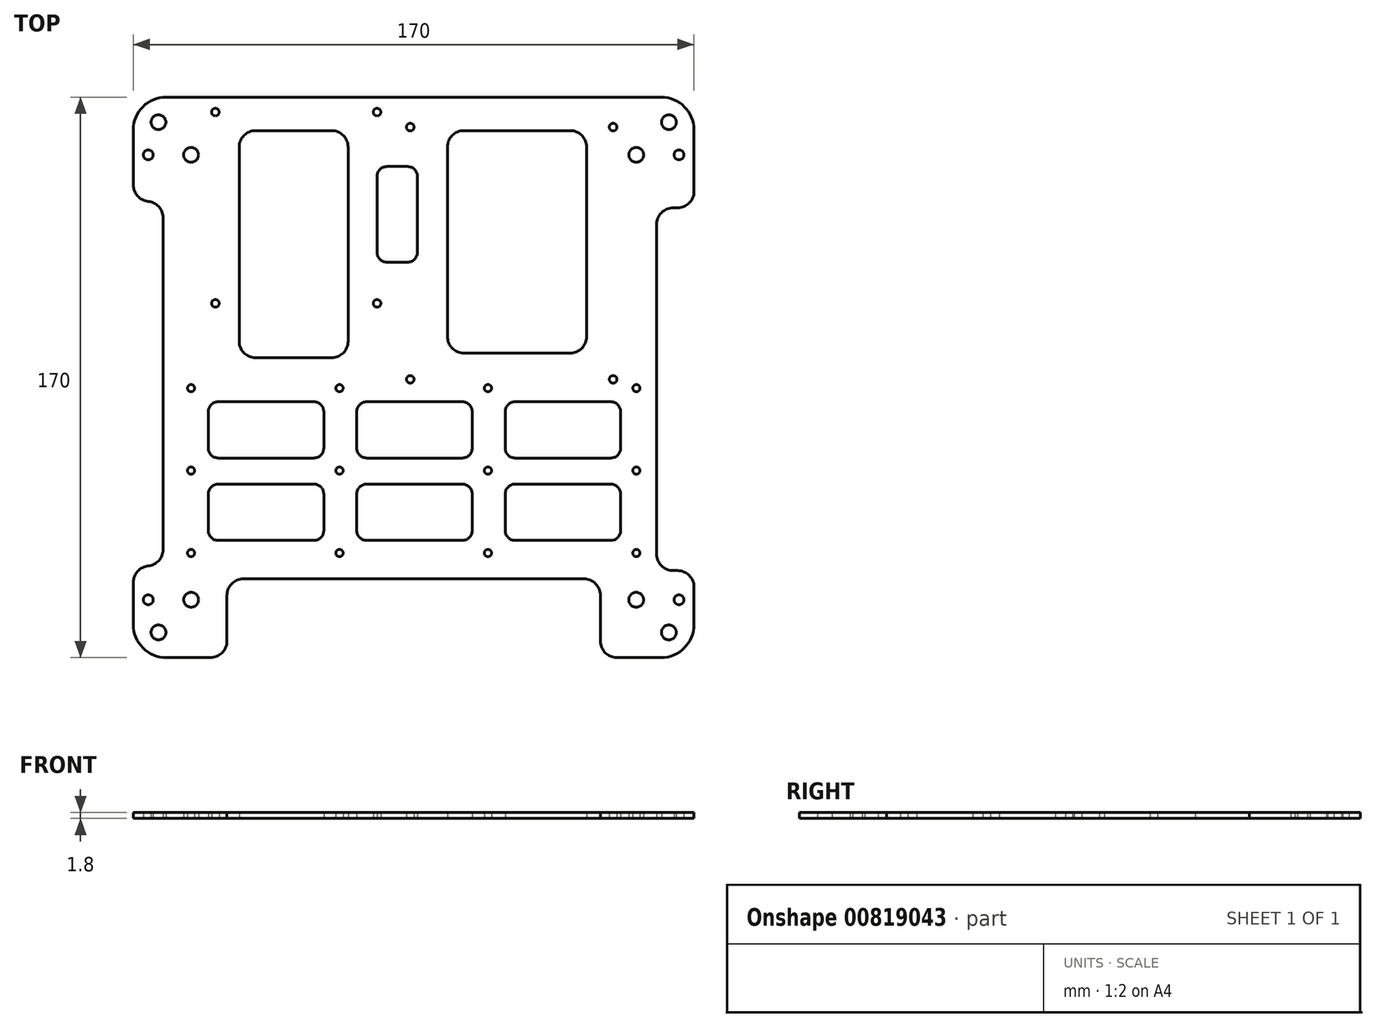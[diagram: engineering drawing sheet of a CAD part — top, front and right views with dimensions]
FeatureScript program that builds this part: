
annotation { "Feature Type Name" : "Feature", "Feature Type Description" : "" }
export const myFeature = defineFeature(function(context is Context, id is Id, definition is map)
    precondition{}
    {
        {
            var Q0;
            Q0=qCreatedBy(makeId("Top.planeOp"),FACE);
            var sketch = newSketch(context, id + "F0", { "sketchPlane" : qUnion([Q0])});
            skLineSegment(sketch, "E0.bottom", {"start": v(-100, -100) * mm, "end": v(100, -100) * mm, "construction": true});
            skLineSegment(sketch, "E0.top", {"start": v(-100, 100) * mm, "end": v(100, 100) * mm, "construction": true});
            skLineSegment(sketch, "E0.left", {"start": v(-100, -100) * mm, "end": v(-100, 100) * mm, "construction": true});
            skLineSegment(sketch, "E0.right", {"start": v(100, -100) * mm, "end": v(100, 100) * mm, "construction": true});
            skPoint(sketch, "E0.middle", {"position": v(0, 0) * mm});
            skCircle(sketch, "E1", {"center": v(-100, 100) * mm, "radius": 2.5 * mm, "construction": true});
            skCircle(sketch, "E2", {"center": v(100, 100) * mm, "radius": 2.5 * mm, "construction": true});
            skCircle(sketch, "E3", {"center": v(100, -100) * mm, "radius": 2.5 * mm, "construction": true});
            skCircle(sketch, "E4", {"center": v(-100, -100) * mm, "radius": 2.5 * mm, "construction": true});
            skLineSegment(sketch, "E5", {"start": v(-100, 100) * mm, "end": v(-77.37, 77.37) * mm, "construction": true});
            skLineSegment(sketch, "E6", {"start": v(-77.37, 77.37) * mm, "end": v(-67.47, 67.47) * mm, "construction": true});
            skCircle(sketch, "E7", {"center": v(-77.37, 77.37) * mm, "radius": 2.25 * mm});
            skCircle(sketch, "E8", {"center": v(-67.47, 67.47) * mm, "radius": 2.25 * mm});
            skLineSegment(sketch, "E9.bottom", {"start": v(-85, 85) * mm, "end": v(85, 85) * mm});
            skLineSegment(sketch, "E9.top", {"start": v(-85, -85) * mm, "end": v(85, -85) * mm});
            skLineSegment(sketch, "E9.left", {"start": v(-85, 85) * mm, "end": v(-85, -85) * mm});
            skLineSegment(sketch, "E9.right", {"start": v(85, 85) * mm, "end": v(85, -85) * mm});
            skLineSegment(sketch, "E10.bottom", {"start": v(-1.03, -0.6) * mm, "end": v(60.47, -0.6) * mm, "construction": true});
            skLineSegment(sketch, "E10.top", {"start": v(-1.03, 75.9) * mm, "end": v(60.47, 75.9) * mm, "construction": true});
            skLineSegment(sketch, "E10.left", {"start": v(-1.03, -0.6) * mm, "end": v(-1.03, 75.9) * mm, "construction": true});
            skLineSegment(sketch, "E10.right", {"start": v(60.47, -0.6) * mm, "end": v(60.47, 75.9) * mm, "construction": true});
            skPoint(sketch, "E10.middle", {"position": v(29.72, 37.64) * mm});
            skLineSegment(sketch, "E11.bottom", {"start": v(-5.28, -12.36) * mm, "end": v(64.72, -12.36) * mm, "construction": true});
            skLineSegment(sketch, "E11.top", {"start": v(-5.28, 87.64) * mm, "end": v(64.72, 87.64) * mm, "construction": true});
            skLineSegment(sketch, "E11.left", {"start": v(-5.28, -12.36) * mm, "end": v(-5.28, 87.64) * mm, "construction": true});
            skLineSegment(sketch, "E11.right", {"start": v(64.72, -12.36) * mm, "end": v(64.72, 87.64) * mm, "construction": true});
            skLineSegment(sketch, "E12.bottom", {"start": v(-11.1, 22.43) * mm, "end": v(-60.1, 22.43) * mm, "construction": true});
            skLineSegment(sketch, "E12.top", {"start": v(-11.1, 80.43) * mm, "end": v(-60.1, 80.43) * mm, "construction": true});
            skLineSegment(sketch, "E12.left", {"start": v(-11.1, 22.43) * mm, "end": v(-11.1, 80.43) * mm, "construction": true});
            skLineSegment(sketch, "E12.right", {"start": v(-60.1, 22.43) * mm, "end": v(-60.1, 80.43) * mm, "construction": true});
            skPoint(sketch, "E12.middle", {"position": v(-35.6, 51.43) * mm});
            skLineSegment(sketch, "E13.bottom", {"start": v(-7.6, 96.43) * mm, "end": v(-63.6, 96.43) * mm, "construction": true});
            skLineSegment(sketch, "E13.top", {"start": v(-7.6, 6.43) * mm, "end": v(-63.6, 6.43) * mm, "construction": true});
            skLineSegment(sketch, "E13.left", {"start": v(-7.6, 96.43) * mm, "end": v(-7.6, 6.43) * mm, "construction": true});
            skLineSegment(sketch, "E13.right", {"start": v(-63.6, 96.43) * mm, "end": v(-63.6, 6.43) * mm, "construction": true});
            skLineSegment(sketch, "E14", {"start": v(0, 0) * mm, "end": v(0, 19) * mm, "construction": true});
            skLineSegment(sketch, "E15", {"start": v(0, 0) * mm, "end": v(16.24, 0) * mm, "construction": true});
            skCircle(sketch, "E16.MirrorC", {"center": v(77.37, 77.37) * mm, "radius": 2.25 * mm});
            skCircle(sketch, "E17.MirrorC", {"center": v(67.47, 67.47) * mm, "radius": 2.25 * mm});
            skCircle(sketch, "E18.MirrorC", {"center": v(-67.47, -67.47) * mm, "radius": 2.25 * mm});
            skCircle(sketch, "E19.MirrorC", {"center": v(-77.37, -77.37) * mm, "radius": 2.25 * mm});
            skCircle(sketch, "E20.MirrorC", {"center": v(77.37, -77.37) * mm, "radius": 2.25 * mm});
            skCircle(sketch, "E21.MirrorC", {"center": v(67.47, -67.47) * mm, "radius": 2.25 * mm});
            skCircle(sketch, "E22", {"center": v(-60.1, 80.43) * mm, "radius": 1.15 * mm});
            skCircle(sketch, "E23", {"center": v(-11.1, 80.43) * mm, "radius": 1.15 * mm});
            skCircle(sketch, "E24", {"center": v(-11.1, 22.43) * mm, "radius": 1.15 * mm});
            skCircle(sketch, "E25", {"center": v(-60.1, 22.43) * mm, "radius": 1.15 * mm});
            skCircle(sketch, "E26", {"center": v(-1.03, 75.9) * mm, "radius": 1.15 * mm});
            skCircle(sketch, "E27", {"center": v(60.47, 75.9) * mm, "radius": 1.15 * mm});
            skCircle(sketch, "E28", {"center": v(60.47, -0.6) * mm, "radius": 1.15 * mm});
            skCircle(sketch, "E29", {"center": v(-1.03, -0.6) * mm, "radius": 1.15 * mm});
            skCircle(sketch, "E30", {"center": v(-80.45, 67.47) * mm, "radius": 1.5 * mm});
            skCircle(sketch, "E31.MirrorC", {"center": v(80.45, 67.47) * mm, "radius": 1.5 * mm});
            skCircle(sketch, "E32.MirrorC", {"center": v(-80.45, -67.47) * mm, "radius": 1.5 * mm});
            skCircle(sketch, "E33.MirrorC", {"center": v(80.45, -67.47) * mm, "radius": 1.5 * mm});
            skSolve(sketch);
        }
        {
            var Q0;
            Q0 = qSketchRegion(id + "F0", true);
            extrude(context, id + "F1", {"entities" : qUnion([Q0]), "depth" : 1.8 * mm, "offsetDistance" : 25 * mm});
        }
        {
            var Q0;
            Q0=makeQuery(id+"F1.opExtrude","SWEPT_EDGE",EDGE,{"disambiguationData":[OSD([sQuery(id+"F0.wireOp",EDGE,"E9.bottom"),sQuery(id+"F0.wireOp",EDGE,"E9.left")])]});
            var Q1;
            Q1=makeQuery(id+"F1.opExtrude","SWEPT_EDGE",EDGE,{"disambiguationData":[OSD([sQuery(id+"F0.wireOp",EDGE,"E9.bottom"),sQuery(id+"F0.wireOp",EDGE,"E9.right")])]});
            var Q2;
            Q2=makeQuery(id+"F1.opExtrude","SWEPT_EDGE",EDGE,{"disambiguationData":[OSD([sQuery(id+"F0.wireOp",EDGE,"E9.top"),sQuery(id+"F0.wireOp",EDGE,"E9.right")])]});
            var Q3;
            Q3=makeQuery(id+"F1.opExtrude","SWEPT_EDGE",EDGE,{"disambiguationData":[OSD([sQuery(id+"F0.wireOp",EDGE,"E9.top"),sQuery(id+"F0.wireOp",EDGE,"E9.left")])]});
            fillet(context, id + "F2", {"entities" : qUnion([Q0, Q1, Q2, Q3]), "radius" : 10 * mm, "tangentPropagation" : true, "allowEdgeOverflow" : false});
        }
        {
            var Q0;
            Q0=qCreatedBy(makeId("Top.planeOp"),FACE);
            var sketch = newSketch(context, id + "F3", { "sketchPlane" : qUnion([Q0])});
            skLineSegment(sketch, "E34", {"start": v(15.24, 7.36) * mm, "end": v(28.1, 7.36) * mm});
            skCircle(sketch, "E35", {"center": v(-67.48, -53.3) * mm, "radius": 1.1 * mm});
            skLineSegment(sketch, "E36", {"start": v(-67.48, -53.3) * mm, "end": v(-67.48, -28.3) * mm, "construction": true});
            skCircle(sketch, "E37", {"center": v(-67.48, -28.3) * mm, "radius": 1.1 * mm});
            skLineSegment(sketch, "E38.bottom", {"start": v(-59.25, -32.4) * mm, "end": v(-30.25, -32.4) * mm});
            skLineSegment(sketch, "E38.top", {"start": v(-59.25, -49.48) * mm, "end": v(-30.25, -49.48) * mm});
            skLineSegment(sketch, "E38.left", {"start": v(-62.25, -35.4) * mm, "end": v(-62.25, -46.48) * mm});
            skLineSegment(sketch, "E38.right", {"start": v(-27.25, -35.4) * mm, "end": v(-27.25, -46.48) * mm});
            skPoint(sketch, "E39.visualSharp", {"position": v(-62.25, -32.4) * mm});
            skArc(sketch, "E39.filletArc", {"start": v(-59.25, -32.4) * mm, "mid": v(-61.37, -33.29) * mm, "end": v(-62.25, -35.4) * mm});
            skPoint(sketch, "E40.visualSharp", {"position": v(-27.25, -32.4) * mm});
            skArc(sketch, "E40.filletArc", {"start": v(-27.25, -35.4) * mm, "mid": v(-28.13, -33.29) * mm, "end": v(-30.25, -32.4) * mm});
            skPoint(sketch, "E41.visualSharp", {"position": v(-27.25, -49.48) * mm});
            skArc(sketch, "E41.filletArc", {"start": v(-30.25, -49.48) * mm, "mid": v(-28.13, -48.6) * mm, "end": v(-27.25, -46.48) * mm});
            skPoint(sketch, "E42.visualSharp", {"position": v(-62.25, -49.48) * mm});
            skArc(sketch, "E42.filletArc", {"start": v(-62.25, -46.48) * mm, "mid": v(-61.37, -48.6) * mm, "end": v(-59.25, -49.48) * mm});
            skLineSegment(sketch, "E43.0.1.0", {"start": v(-27.25, -10.4) * mm, "end": v(-27.25, -21.48) * mm});
            skLineSegment(sketch, "E43.0.1.1", {"start": v(-59.25, -7.4) * mm, "end": v(-30.25, -7.4) * mm});
            skLineSegment(sketch, "E43.0.1.2", {"start": v(-67.48, -28.3) * mm, "end": v(-67.48, -3.3) * mm, "construction": true});
            skLineSegment(sketch, "E43.0.1.3", {"start": v(-62.25, -10.4) * mm, "end": v(-62.25, -21.48) * mm});
            skLineSegment(sketch, "E43.0.1.4", {"start": v(-59.25, -24.48) * mm, "end": v(-30.25, -24.48) * mm});
            skPoint(sketch, "E43.0.1.5", {"position": v(-62.25, -24.48) * mm});
            skPoint(sketch, "E43.0.1.6", {"position": v(-27.25, -24.48) * mm});
            skPoint(sketch, "E43.0.1.7", {"position": v(-27.25, -7.4) * mm});
            skPoint(sketch, "E43.0.1.8", {"position": v(-62.25, -7.4) * mm});
            skArc(sketch, "E43.0.1.9", {"start": v(-59.25, -7.4) * mm, "mid": v(-61.37, -8.29) * mm, "end": v(-62.25, -10.4) * mm});
            skArc(sketch, "E43.0.1.10", {"start": v(-30.25, -24.48) * mm, "mid": v(-28.13, -23.6) * mm, "end": v(-27.25, -21.48) * mm});
            skArc(sketch, "E43.0.1.11", {"start": v(-62.25, -21.48) * mm, "mid": v(-61.37, -23.6) * mm, "end": v(-59.25, -24.48) * mm});
            skCircle(sketch, "E43.0.1.12", {"center": v(-67.48, -3.3) * mm, "radius": 1.1 * mm});
            skArc(sketch, "E43.0.1.14", {"start": v(-27.25, -10.4) * mm, "mid": v(-28.13, -8.29) * mm, "end": v(-30.25, -7.4) * mm});
            skLineSegment(sketch, "E43.1.0.0", {"start": v(17.75, -35.4) * mm, "end": v(17.75, -46.48) * mm});
            skLineSegment(sketch, "E43.1.0.1", {"start": v(-14.25, -32.4) * mm, "end": v(14.75, -32.4) * mm});
            skLineSegment(sketch, "E43.1.0.2", {"start": v(-22.48, -53.3) * mm, "end": v(-22.48, -28.3) * mm, "construction": true});
            skLineSegment(sketch, "E43.1.0.3", {"start": v(-17.25, -35.4) * mm, "end": v(-17.25, -46.48) * mm});
            skLineSegment(sketch, "E43.1.0.4", {"start": v(-14.25, -49.48) * mm, "end": v(14.75, -49.48) * mm});
            skPoint(sketch, "E43.1.0.5", {"position": v(-17.25, -49.48) * mm});
            skPoint(sketch, "E43.1.0.6", {"position": v(17.75, -49.48) * mm});
            skPoint(sketch, "E43.1.0.7", {"position": v(17.75, -32.4) * mm});
            skPoint(sketch, "E43.1.0.8", {"position": v(-17.25, -32.4) * mm});
            skArc(sketch, "E43.1.0.9", {"start": v(-14.25, -32.4) * mm, "mid": v(-16.37, -33.29) * mm, "end": v(-17.25, -35.4) * mm});
            skArc(sketch, "E43.1.0.10", {"start": v(14.75, -49.48) * mm, "mid": v(16.87, -48.6) * mm, "end": v(17.75, -46.48) * mm});
            skArc(sketch, "E43.1.0.11", {"start": v(-17.25, -46.48) * mm, "mid": v(-16.37, -48.6) * mm, "end": v(-14.25, -49.48) * mm});
            skCircle(sketch, "E43.1.0.12", {"center": v(-22.48, -28.3) * mm, "radius": 1.1 * mm});
            skCircle(sketch, "E43.1.0.13", {"center": v(-22.48, -53.3) * mm, "radius": 1.1 * mm});
            skArc(sketch, "E43.1.0.14", {"start": v(17.75, -35.4) * mm, "mid": v(16.87, -33.29) * mm, "end": v(14.75, -32.4) * mm});
            skLineSegment(sketch, "E43.1.1.0", {"start": v(17.75, -10.4) * mm, "end": v(17.75, -21.48) * mm});
            skLineSegment(sketch, "E43.1.1.1", {"start": v(-14.25, -7.4) * mm, "end": v(14.75, -7.4) * mm});
            skLineSegment(sketch, "E43.1.1.2", {"start": v(-22.48, -28.3) * mm, "end": v(-22.48, -3.3) * mm, "construction": true});
            skLineSegment(sketch, "E43.1.1.3", {"start": v(-17.25, -10.4) * mm, "end": v(-17.25, -21.48) * mm});
            skLineSegment(sketch, "E43.1.1.4", {"start": v(-14.25, -24.48) * mm, "end": v(14.75, -24.48) * mm});
            skPoint(sketch, "E43.1.1.5", {"position": v(-17.25, -24.48) * mm});
            skPoint(sketch, "E43.1.1.6", {"position": v(17.75, -24.48) * mm});
            skPoint(sketch, "E43.1.1.7", {"position": v(17.75, -7.4) * mm});
            skPoint(sketch, "E43.1.1.8", {"position": v(-17.25, -7.4) * mm});
            skArc(sketch, "E43.1.1.9", {"start": v(-14.25, -7.4) * mm, "mid": v(-16.37, -8.29) * mm, "end": v(-17.25, -10.4) * mm});
            skArc(sketch, "E43.1.1.10", {"start": v(14.75, -24.48) * mm, "mid": v(16.87, -23.6) * mm, "end": v(17.75, -21.48) * mm});
            skArc(sketch, "E43.1.1.11", {"start": v(-17.25, -21.48) * mm, "mid": v(-16.37, -23.6) * mm, "end": v(-14.25, -24.48) * mm});
            skCircle(sketch, "E43.1.1.12", {"center": v(-22.48, -3.3) * mm, "radius": 1.1 * mm});
            skCircle(sketch, "E43.1.1.13", {"center": v(-22.48, -28.3) * mm, "radius": 1.1 * mm});
            skArc(sketch, "E43.1.1.14", {"start": v(17.75, -10.4) * mm, "mid": v(16.87, -8.29) * mm, "end": v(14.75, -7.4) * mm});
            skLineSegment(sketch, "E43.2.0.0", {"start": v(62.75, -35.4) * mm, "end": v(62.75, -46.48) * mm});
            skLineSegment(sketch, "E43.2.0.1", {"start": v(30.75, -32.4) * mm, "end": v(59.75, -32.4) * mm});
            skLineSegment(sketch, "E43.2.0.2", {"start": v(22.52, -53.3) * mm, "end": v(22.52, -28.3) * mm, "construction": true});
            skLineSegment(sketch, "E43.2.0.3", {"start": v(27.75, -35.4) * mm, "end": v(27.75, -46.48) * mm});
            skLineSegment(sketch, "E43.2.0.4", {"start": v(30.75, -49.48) * mm, "end": v(59.75, -49.48) * mm});
            skPoint(sketch, "E43.2.0.5", {"position": v(27.75, -49.48) * mm});
            skPoint(sketch, "E43.2.0.6", {"position": v(62.75, -49.48) * mm});
            skPoint(sketch, "E43.2.0.7", {"position": v(62.75, -32.4) * mm});
            skPoint(sketch, "E43.2.0.8", {"position": v(27.75, -32.4) * mm});
            skArc(sketch, "E43.2.0.9", {"start": v(30.75, -32.4) * mm, "mid": v(28.63, -33.29) * mm, "end": v(27.75, -35.4) * mm});
            skArc(sketch, "E43.2.0.10", {"start": v(59.75, -49.48) * mm, "mid": v(61.87, -48.6) * mm, "end": v(62.75, -46.48) * mm});
            skArc(sketch, "E43.2.0.11", {"start": v(27.75, -46.48) * mm, "mid": v(28.63, -48.6) * mm, "end": v(30.75, -49.48) * mm});
            skCircle(sketch, "E43.2.0.12", {"center": v(22.52, -28.3) * mm, "radius": 1.1 * mm});
            skCircle(sketch, "E43.2.0.13", {"center": v(22.52, -53.3) * mm, "radius": 1.1 * mm});
            skArc(sketch, "E43.2.0.14", {"start": v(62.75, -35.4) * mm, "mid": v(61.87, -33.29) * mm, "end": v(59.75, -32.4) * mm});
            skLineSegment(sketch, "E43.2.1.0", {"start": v(62.75, -10.4) * mm, "end": v(62.75, -21.48) * mm});
            skLineSegment(sketch, "E43.2.1.1", {"start": v(30.75, -7.4) * mm, "end": v(59.75, -7.4) * mm});
            skLineSegment(sketch, "E43.2.1.2", {"start": v(22.52, -28.3) * mm, "end": v(22.52, -3.3) * mm, "construction": true});
            skLineSegment(sketch, "E43.2.1.3", {"start": v(27.75, -10.4) * mm, "end": v(27.75, -21.48) * mm});
            skLineSegment(sketch, "E43.2.1.4", {"start": v(30.75, -24.48) * mm, "end": v(59.75, -24.48) * mm});
            skPoint(sketch, "E43.2.1.5", {"position": v(27.75, -24.48) * mm});
            skPoint(sketch, "E43.2.1.6", {"position": v(62.75, -24.48) * mm});
            skPoint(sketch, "E43.2.1.7", {"position": v(62.75, -7.4) * mm});
            skPoint(sketch, "E43.2.1.8", {"position": v(27.75, -7.4) * mm});
            skArc(sketch, "E43.2.1.9", {"start": v(30.75, -7.4) * mm, "mid": v(28.63, -8.29) * mm, "end": v(27.75, -10.4) * mm});
            skArc(sketch, "E43.2.1.10", {"start": v(59.75, -24.48) * mm, "mid": v(61.87, -23.6) * mm, "end": v(62.75, -21.48) * mm});
            skArc(sketch, "E43.2.1.11", {"start": v(27.75, -21.48) * mm, "mid": v(28.63, -23.6) * mm, "end": v(30.75, -24.48) * mm});
            skCircle(sketch, "E43.2.1.12", {"center": v(22.52, -3.3) * mm, "radius": 1.1 * mm});
            skCircle(sketch, "E43.2.1.13", {"center": v(22.52, -28.3) * mm, "radius": 1.1 * mm});
            skArc(sketch, "E43.2.1.14", {"start": v(62.75, -10.4) * mm, "mid": v(61.87, -8.29) * mm, "end": v(59.75, -7.4) * mm});
            skLineSegment(sketch, "E43.3.0.0", {"start": v(107.75, -35.4) * mm, "end": v(107.75, -46.48) * mm, "construction": true});
            skLineSegment(sketch, "E43.3.0.1", {"start": v(75.75, -32.4) * mm, "end": v(104.75, -32.4) * mm, "construction": true});
            skLineSegment(sketch, "E43.3.0.2", {"start": v(67.52, -53.3) * mm, "end": v(67.52, -28.3) * mm, "construction": true});
            skLineSegment(sketch, "E43.3.0.3", {"start": v(72.75, -35.4) * mm, "end": v(72.75, -46.48) * mm, "construction": true});
            skLineSegment(sketch, "E43.3.0.4", {"start": v(75.75, -49.48) * mm, "end": v(104.75, -49.48) * mm, "construction": true});
            skPoint(sketch, "E43.3.0.5", {"position": v(72.75, -49.48) * mm});
            skPoint(sketch, "E43.3.0.6", {"position": v(107.75, -49.48) * mm});
            skPoint(sketch, "E43.3.0.7", {"position": v(107.75, -32.4) * mm});
            skPoint(sketch, "E43.3.0.8", {"position": v(72.75, -32.4) * mm});
            skArc(sketch, "E43.3.0.9", {"start": v(75.75, -32.4) * mm, "mid": v(73.63, -33.29) * mm, "end": v(72.75, -35.4) * mm, "construction": true});
            skArc(sketch, "E43.3.0.10", {"start": v(104.75, -49.48) * mm, "mid": v(106.87, -48.6) * mm, "end": v(107.75, -46.48) * mm, "construction": true});
            skArc(sketch, "E43.3.0.11", {"start": v(72.75, -46.48) * mm, "mid": v(73.63, -48.6) * mm, "end": v(75.75, -49.48) * mm, "construction": true});
            skCircle(sketch, "E43.3.0.12", {"center": v(67.52, -28.3) * mm, "radius": 1.1 * mm});
            skCircle(sketch, "E43.3.0.13", {"center": v(67.52, -53.3) * mm, "radius": 1.1 * mm});
            skArc(sketch, "E43.3.0.14", {"start": v(107.75, -35.4) * mm, "mid": v(106.87, -33.29) * mm, "end": v(104.75, -32.4) * mm, "construction": true});
            skLineSegment(sketch, "E43.3.1.0", {"start": v(107.75, -10.4) * mm, "end": v(107.75, -21.48) * mm, "construction": true});
            skLineSegment(sketch, "E43.3.1.1", {"start": v(75.75, -7.4) * mm, "end": v(104.75, -7.4) * mm, "construction": true});
            skLineSegment(sketch, "E43.3.1.2", {"start": v(67.52, -28.3) * mm, "end": v(67.52, -3.3) * mm, "construction": true});
            skLineSegment(sketch, "E43.3.1.3", {"start": v(72.75, -10.4) * mm, "end": v(72.75, -21.48) * mm, "construction": true});
            skLineSegment(sketch, "E43.3.1.4", {"start": v(75.75, -24.48) * mm, "end": v(104.75, -24.48) * mm, "construction": true});
            skPoint(sketch, "E43.3.1.5", {"position": v(72.75, -24.48) * mm});
            skPoint(sketch, "E43.3.1.6", {"position": v(107.75, -24.48) * mm});
            skPoint(sketch, "E43.3.1.7", {"position": v(107.75, -7.4) * mm});
            skPoint(sketch, "E43.3.1.8", {"position": v(72.75, -7.4) * mm});
            skArc(sketch, "E43.3.1.9", {"start": v(75.75, -7.4) * mm, "mid": v(73.63, -8.29) * mm, "end": v(72.75, -10.4) * mm, "construction": true});
            skArc(sketch, "E43.3.1.10", {"start": v(104.75, -24.48) * mm, "mid": v(106.87, -23.6) * mm, "end": v(107.75, -21.48) * mm, "construction": true});
            skArc(sketch, "E43.3.1.11", {"start": v(72.75, -21.48) * mm, "mid": v(73.63, -23.6) * mm, "end": v(75.75, -24.48) * mm, "construction": true});
            skCircle(sketch, "E43.3.1.12", {"center": v(67.52, -3.3) * mm, "radius": 1.1 * mm});
            skCircle(sketch, "E43.3.1.13", {"center": v(67.52, -28.3) * mm, "radius": 1.1 * mm});
            skArc(sketch, "E43.3.1.14", {"start": v(107.75, -10.4) * mm, "mid": v(106.87, -8.29) * mm, "end": v(104.75, -7.4) * mm, "construction": true});
            skLineSegment(sketch, "E43.direction1", {"start": v(-67.48, -53.3) * mm, "end": v(-22.48, -53.3) * mm, "construction": true});
            skLineSegment(sketch, "E44", {"start": v(28.1, 7.36) * mm, "end": v(47.45, 7.36) * mm});
            skLineSegment(sketch, "E45", {"start": v(52.45, 12.36) * mm, "end": v(52.45, 69.83) * mm});
            skLineSegment(sketch, "E46", {"start": v(47.45, 74.83) * mm, "end": v(15.24, 74.83) * mm});
            skLineSegment(sketch, "E47", {"start": v(-52.9, 69.83) * mm, "end": v(-52.9, 10.94) * mm});
            skLineSegment(sketch, "E48", {"start": v(-47.9, 5.94) * mm, "end": v(-24.88, 5.94) * mm});
            skLineSegment(sketch, "E49", {"start": v(10.24, 30.17) * mm, "end": v(10.24, 12.36) * mm});
            skPoint(sketch, "E50.orphan", {"position": v(28.1, 5.94) * mm});
            skPoint(sketch, "E51.visualSharp", {"position": v(-52.9, 74.83) * mm});
            skArc(sketch, "E51.filletArc", {"start": v(-47.9, 74.83) * mm, "mid": v(-51.43, 73.37) * mm, "end": v(-52.9, 69.83) * mm});
            skPoint(sketch, "E52.visualSharp", {"position": v(52.45, 74.83) * mm});
            skArc(sketch, "E52.filletArc", {"start": v(52.45, 69.83) * mm, "mid": v(50.98, 73.37) * mm, "end": v(47.45, 74.83) * mm});
            skPoint(sketch, "E53.visualSharp", {"position": v(52.45, 7.36) * mm});
            skArc(sketch, "E53.filletArc", {"start": v(47.45, 7.36) * mm, "mid": v(50.98, 8.82) * mm, "end": v(52.45, 12.36) * mm});
            skPoint(sketch, "E54.visualSharp", {"position": v(10.24, 7.36) * mm});
            skArc(sketch, "E54.filletArc", {"start": v(10.24, 12.36) * mm, "mid": v(11.7, 8.82) * mm, "end": v(15.24, 7.36) * mm});
            skPoint(sketch, "E55.visualSharp", {"position": v(-52.9, 5.94) * mm});
            skArc(sketch, "E55.filletArc", {"start": v(-52.9, 10.94) * mm, "mid": v(-51.43, 7.4) * mm, "end": v(-47.9, 5.94) * mm});
            skPoint(sketch, "E56.visualSharp", {"position": v(10.24, 5.94) * mm});
            skLineSegment(sketch, "E57", {"start": v(-19.88, 10.94) * mm, "end": v(-19.88, 69.83) * mm});
            skLineSegment(sketch, "E58", {"start": v(10.24, 30.17) * mm, "end": v(10.24, 69.83) * mm});
            skLineSegment(sketch, "E59.trimOffspring", {"start": v(-24.88, 74.83) * mm, "end": v(-47.9, 74.83) * mm});
            skPoint(sketch, "E60.visualSharp", {"position": v(10.24, 74.83) * mm});
            skArc(sketch, "E60.filletArc", {"start": v(15.24, 74.83) * mm, "mid": v(11.7, 73.37) * mm, "end": v(10.24, 69.83) * mm});
            skPoint(sketch, "E61.visualSharp", {"position": v(-19.88, 74.83) * mm});
            skArc(sketch, "E61.filletArc", {"start": v(-19.88, 69.83) * mm, "mid": v(-21.34, 73.37) * mm, "end": v(-24.88, 74.83) * mm});
            skPoint(sketch, "E62.visualSharp", {"position": v(-19.88, 5.94) * mm});
            skArc(sketch, "E62.filletArc", {"start": v(-24.88, 5.94) * mm, "mid": v(-21.34, 7.4) * mm, "end": v(-19.88, 10.94) * mm});
            skLineSegment(sketch, "E63.bottom", {"start": v(-1.84, 34.94) * mm, "end": v(-8.12, 34.94) * mm});
            skLineSegment(sketch, "E63.top", {"start": v(-1.84, 63.92) * mm, "end": v(-8.12, 63.92) * mm});
            skLineSegment(sketch, "E63.left", {"start": v(1.16, 37.94) * mm, "end": v(1.16, 60.92) * mm});
            skLineSegment(sketch, "E63.right", {"start": v(-11.12, 37.94) * mm, "end": v(-11.12, 60.92) * mm});
            skPoint(sketch, "E63.middle", {"position": v(-4.98, 49.43) * mm});
            skPoint(sketch, "E64.visualSharp", {"position": v(-11.12, 63.92) * mm});
            skArc(sketch, "E64.filletArc", {"start": v(-8.12, 63.92) * mm, "mid": v(-10.24, 63.05) * mm, "end": v(-11.12, 60.92) * mm});
            skPoint(sketch, "E65.visualSharp", {"position": v(-11.12, 34.94) * mm});
            skArc(sketch, "E65.filletArc", {"start": v(-11.12, 37.94) * mm, "mid": v(-10.24, 35.82) * mm, "end": v(-8.12, 34.94) * mm});
            skPoint(sketch, "E66.visualSharp", {"position": v(1.16, 34.94) * mm});
            skArc(sketch, "E66.filletArc", {"start": v(-1.84, 34.94) * mm, "mid": v(0.28, 35.82) * mm, "end": v(1.16, 37.94) * mm});
            skPoint(sketch, "E67.visualSharp", {"position": v(1.16, 63.92) * mm});
            skArc(sketch, "E67.filletArc", {"start": v(1.16, 60.92) * mm, "mid": v(0.28, 63.05) * mm, "end": v(-1.84, 63.92) * mm});
            skLineSegment(sketch, "E68.bottom", {"start": v(-81, 53.4) * mm, "end": v(-120.52, 53.4) * mm});
            skLineSegment(sketch, "E68.top", {"start": v(-81, -57.25) * mm, "end": v(-120.52, -57.25) * mm});
            skLineSegment(sketch, "E68.left", {"start": v(-76, 48.4) * mm, "end": v(-76, -52.25) * mm});
            skLineSegment(sketch, "E68.right", {"start": v(-120.52, 53.4) * mm, "end": v(-120.52, -57.25) * mm});
            skPoint(sketch, "E68.middle", {"position": v(-98.26, -1.93) * mm});
            skLineSegment(sketch, "E69.bottom", {"start": v(78.67, 51.4) * mm, "end": v(100.25, 51.4) * mm});
            skLineSegment(sketch, "E69.top", {"start": v(78.67, -58.63) * mm, "end": v(100.25, -58.63) * mm});
            skLineSegment(sketch, "E69.left", {"start": v(73.67, 46.4) * mm, "end": v(73.67, -53.63) * mm});
            skLineSegment(sketch, "E69.right", {"start": v(100.25, 51.4) * mm, "end": v(100.25, -58.63) * mm});
            skPoint(sketch, "E69.middle", {"position": v(86.96, -3.6) * mm});
            skPoint(sketch, "E70.visualSharp", {"position": v(73.67, 51.4) * mm});
            skArc(sketch, "E70.filletArc", {"start": v(78.67, 51.4) * mm, "mid": v(75.13, 49.94) * mm, "end": v(73.67, 46.4) * mm});
            skPoint(sketch, "E71.visualSharp", {"position": v(73.67, -58.63) * mm});
            skArc(sketch, "E71.filletArc", {"start": v(73.67, -53.63) * mm, "mid": v(75.13, -57.16) * mm, "end": v(78.67, -58.63) * mm});
            skArc(sketch, "E72.filletArc", {"start": v(-76, 48.4) * mm, "mid": v(-77.46, 51.93) * mm, "end": v(-81, 53.4) * mm});
            skPoint(sketch, "E73.visualSharp", {"position": v(-76, -57.25) * mm});
            skArc(sketch, "E73.filletArc", {"start": v(-81, -57.25) * mm, "mid": v(-77.46, -55.79) * mm, "end": v(-76, -52.25) * mm});
            skLineSegment(sketch, "E74.bottom", {"start": v(56.61, -98.87) * mm, "end": v(-56.61, -98.87) * mm});
            skLineSegment(sketch, "E74.top", {"start": v(51.61, -61.14) * mm, "end": v(-51.61, -61.14) * mm});
            skLineSegment(sketch, "E74.left", {"start": v(56.61, -98.87) * mm, "end": v(56.61, -66.14) * mm});
            skLineSegment(sketch, "E74.right", {"start": v(-56.61, -98.87) * mm, "end": v(-56.61, -66.14) * mm});
            skPoint(sketch, "E74.middle", {"position": v(0, -80) * mm});
            skPoint(sketch, "E75.visualSharp", {"position": v(-56.61, -61.14) * mm});
            skArc(sketch, "E75.filletArc", {"start": v(-51.61, -61.14) * mm, "mid": v(-55.15, -62.6) * mm, "end": v(-56.61, -66.14) * mm});
            skPoint(sketch, "E76.visualSharp", {"position": v(56.61, -61.14) * mm});
            skArc(sketch, "E76.filletArc", {"start": v(56.61, -66.14) * mm, "mid": v(55.15, -62.6) * mm, "end": v(51.61, -61.14) * mm});
            skSolve(sketch);
        }
        {
            var Q0;
            Q0 = qSketchRegion(id + "F3", true);
            extrude(context, id + "F4", {"entities" : qUnion([Q0]), "operationType" : NewBodyOperationType.REMOVE, "depth" : 25 * mm, "offsetDistance" : 25 * mm});
        }
        {
            var Q0;
            Q0=makeQuery(id+"F4.boolean.opBoolean","INTERSECT",EDGE,{"derivedFrom":[makeQuery(id+"F1.opExtrude","SWEPT_FACE",FACE,{"disambiguationData":[OSD([sQuery(id+"F0.wireOp",EDGE,"E9.right")])]}),makeQuery(id+"F4.opExtrude","SWEPT_FACE",FACE,{"disambiguationData":[OSD([sQuery(id+"F3.wireOp",EDGE,"E69.bottom")])]})]});
            var Q1;
            Q1=makeQuery(id+"F4.boolean.opBoolean","INTERSECT",EDGE,{"derivedFrom":[makeQuery(id+"F1.opExtrude","SWEPT_FACE",FACE,{"disambiguationData":[OSD([sQuery(id+"F0.wireOp",EDGE,"E9.right")])]}),makeQuery(id+"F4.opExtrude","SWEPT_FACE",FACE,{"disambiguationData":[OSD([sQuery(id+"F3.wireOp",EDGE,"E69.top")])]})]});
            var Q2;
            Q2=makeQuery(id+"F4.boolean.opBoolean","INTERSECT",EDGE,{"derivedFrom":[makeQuery(id+"F1.opExtrude","SWEPT_FACE",FACE,{"disambiguationData":[OSD([sQuery(id+"F0.wireOp",EDGE,"E9.left")])]}),makeQuery(id+"F4.opExtrude","SWEPT_FACE",FACE,{"disambiguationData":[OSD([sQuery(id+"F3.wireOp",EDGE,"E68.top")])]})]});
            var Q3;
            Q3=makeQuery(id+"F4.boolean.opBoolean","INTERSECT",EDGE,{"derivedFrom":[makeQuery(id+"F1.opExtrude","SWEPT_FACE",FACE,{"disambiguationData":[OSD([sQuery(id+"F0.wireOp",EDGE,"E9.left")])]}),makeQuery(id+"F4.opExtrude","SWEPT_FACE",FACE,{"disambiguationData":[OSD([sQuery(id+"F3.wireOp",EDGE,"E68.bottom")])]})]});
            var Q4;
            Q4=makeQuery(id+"F4.boolean.opBoolean","INTERSECT",EDGE,{"derivedFrom":[makeQuery(id+"F1.opExtrude","SWEPT_FACE",FACE,{"disambiguationData":[OSD([sQuery(id+"F0.wireOp",EDGE,"E9.top")])]}),makeQuery(id+"F4.opExtrude","SWEPT_FACE",FACE,{"disambiguationData":[OSD([sQuery(id+"F3.wireOp",EDGE,"E74.right")])]})]});
            var Q5;
            Q5=makeQuery(id+"F4.boolean.opBoolean","INTERSECT",EDGE,{"derivedFrom":[makeQuery(id+"F1.opExtrude","SWEPT_FACE",FACE,{"disambiguationData":[OSD([sQuery(id+"F0.wireOp",EDGE,"E9.top")])]}),makeQuery(id+"F4.opExtrude","SWEPT_FACE",FACE,{"disambiguationData":[OSD([sQuery(id+"F3.wireOp",EDGE,"E74.left")])]})]});
            fillet(context, id + "F5", {"entities" : qUnion([Q0, Q1, Q2, Q3, Q4, Q5]), "radius" : 5 * mm, "tangentPropagation" : true, "allowEdgeOverflow" : false});
        }
    });
